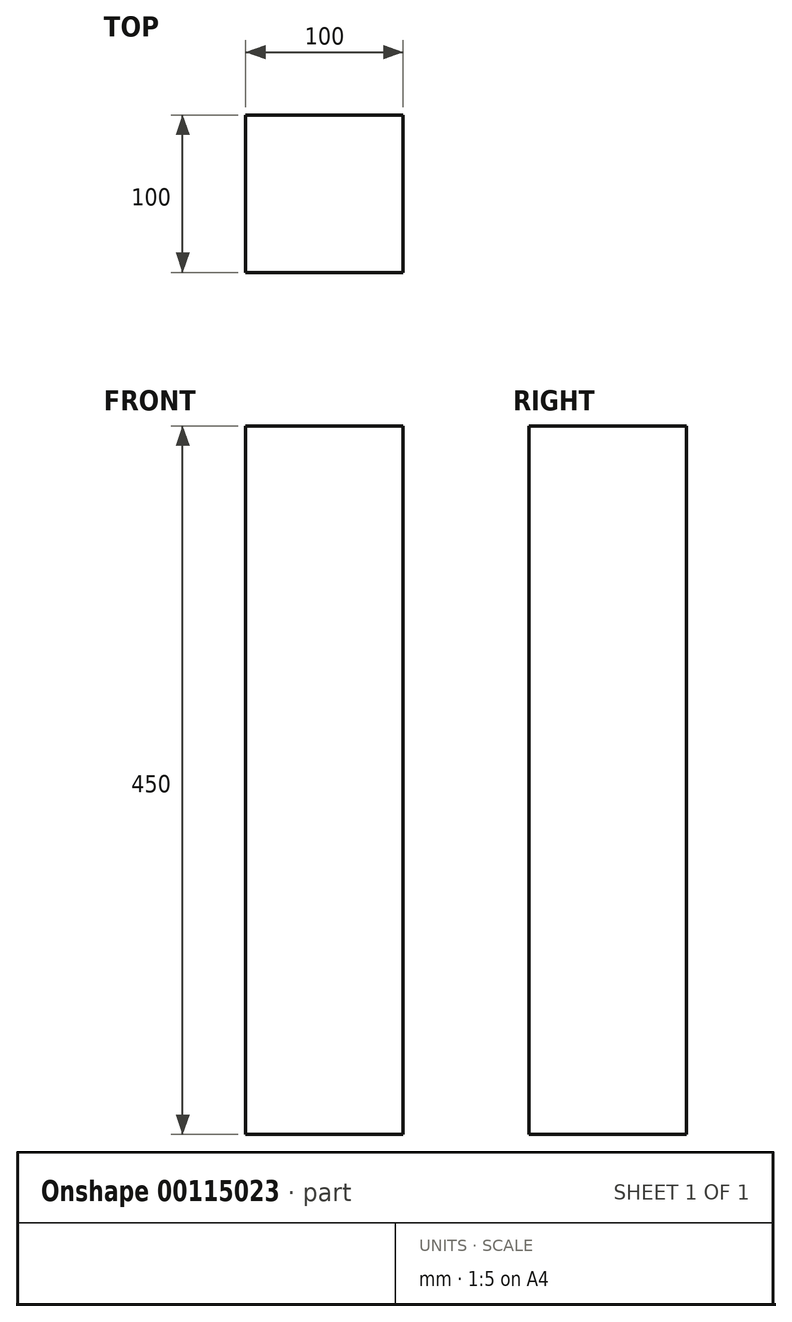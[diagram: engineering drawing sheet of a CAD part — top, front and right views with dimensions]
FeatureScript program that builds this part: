
annotation { "Feature Type Name" : "Feature", "Feature Type Description" : "" }
export const myFeature = defineFeature(function(context is Context, id is Id, definition is map)
    precondition{}
    {
        {
            var Q0;
            Q0=qCreatedBy(makeId("Top.planeOp"),FACE);
            var sketch = newSketch(context, id + "F0", { "sketchPlane" : qUnion([Q0])});
            skLineSegment(sketch, "E0.bottom", {"start": v(50, -50) * mm, "end": v(-50, -50) * mm});
            skLineSegment(sketch, "E0.top", {"start": v(50, 50) * mm, "end": v(-50, 50) * mm});
            skLineSegment(sketch, "E0.left", {"start": v(50, -50) * mm, "end": v(50, 50) * mm});
            skLineSegment(sketch, "E0.right", {"start": v(-50, -50) * mm, "end": v(-50, 50) * mm});
            skPoint(sketch, "E0.middle", {"position": v(0, 0) * mm});
            skSolve(sketch);
        }
        {
            var Q0;
            Q0 = qSketchRegion(id + "F0", true);
            extrude(context, id + "F1", {"entities" : qUnion([Q0]), "depth" : 450 * mm});
        }
    });
